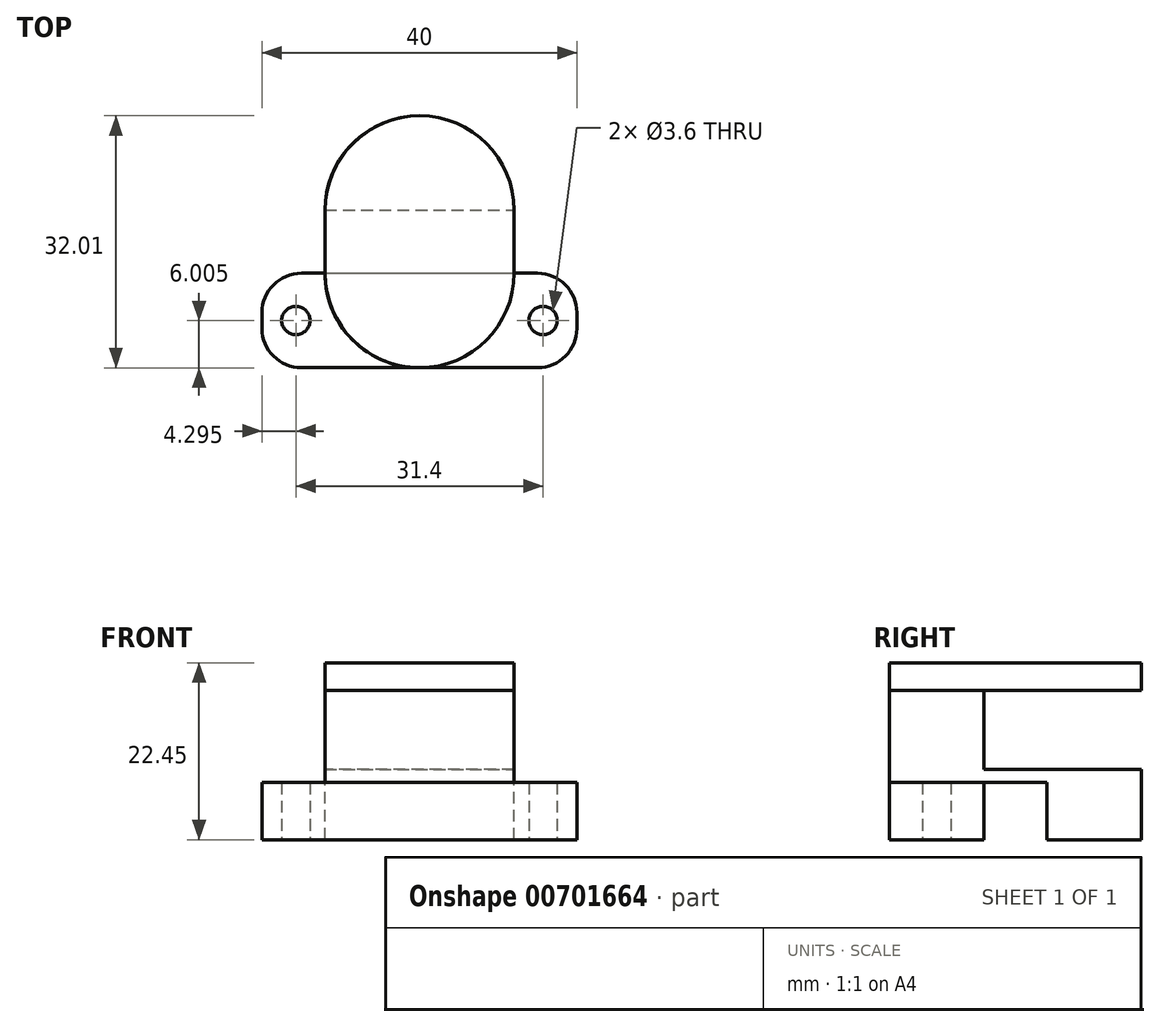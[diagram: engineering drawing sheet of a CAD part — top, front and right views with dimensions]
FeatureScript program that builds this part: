
annotation { "Feature Type Name" : "Feature", "Feature Type Description" : "" }
export const myFeature = defineFeature(function(context is Context, id is Id, definition is map)
    precondition{}
    {
        {
            var Q0;
            Q0=qCreatedBy(makeId("Top.planeOp"),FACE);
            var sketch = newSketch(context, id + "F0", { "sketchPlane" : qUnion([Q0])});
            skLineSegment(sketch, "E0.bottom", {"start": v(-15.42, -8.49) * mm, "end": v(14.58, -8.49) * mm});
            skLineSegment(sketch, "E0.top", {"start": v(-15.42, -20.49) * mm, "end": v(14.58, -20.49) * mm});
            skLineSegment(sketch, "E0.left", {"start": v(-20.42, -13.49) * mm, "end": v(-20.42, -15.49) * mm});
            skLineSegment(sketch, "E0.right", {"start": v(19.58, -13.49) * mm, "end": v(19.58, -15.49) * mm});
            skPoint(sketch, "E1.visualSharp", {"position": v(-20.42, -20.49) * mm});
            skArc(sketch, "E1.filletArc", {"start": v(-20.42, -15.49) * mm, "mid": v(-18.96, -19.02) * mm, "end": v(-15.42, -20.49) * mm});
            skPoint(sketch, "E2.visualSharp", {"position": v(-20.42, -8.49) * mm});
            skArc(sketch, "E2.filletArc", {"start": v(-15.42, -8.49) * mm, "mid": v(-18.96, -9.95) * mm, "end": v(-20.42, -13.49) * mm});
            skPoint(sketch, "E3.visualSharp", {"position": v(19.58, -20.49) * mm});
            skArc(sketch, "E3.filletArc", {"start": v(14.58, -20.49) * mm, "mid": v(18.11, -19.02) * mm, "end": v(19.58, -15.49) * mm});
            skPoint(sketch, "E4.visualSharp", {"position": v(19.58, -8.49) * mm});
            skArc(sketch, "E4.filletArc", {"start": v(19.58, -13.49) * mm, "mid": v(18.11, -9.95) * mm, "end": v(14.58, -8.49) * mm});
            skPoint(sketch, "E5.centerSnap0", {"position": v(-20.42, -14.49) * mm});
            skCircle(sketch, "E6", {"center": v(-16.12, -14.49) * mm, "radius": 1.8 * mm});
            skCircle(sketch, "E7", {"center": v(15.28, -14.49) * mm, "radius": 1.8 * mm});
            skSolve(sketch);
        }
        {
            var Q0;
            Q0 = qSketchRegion(id + "F0", true);
            extrude(context, id + "F1", {"entities" : qUnion([Q0]), "depth" : 7.25 * mm, "offsetDistance" : 25 * mm});
        }
        {
            var Q0;
            Q0=makeQuery(id+"F1.opExtrude","CAP_FACE",FACE,{"disambiguationData":[OSD([sQuery(id+"F0.wireOp",EDGE,"E0.bottom"),sQuery(id+"F0.wireOp",EDGE,"E0.top"),sQuery(id+"F0.wireOp",EDGE,"E0.left"),sQuery(id+"F0.wireOp",EDGE,"E0.right"),sQuery(id+"F0.wireOp",EDGE,"E1.filletArc"),sQuery(id+"F0.wireOp",EDGE,"E2.filletArc"),sQuery(id+"F0.wireOp",EDGE,"E3.filletArc"),sQuery(id+"F0.wireOp",EDGE,"E4.filletArc"),sQuery(id+"F0.wireOp",EDGE,"E6"),sQuery(id+"F0.wireOp",EDGE,"E7")])],"isStart":false});
            var sketch = newSketch(context, id + "F2", { "sketchPlane" : qUnion([Q0])});
            skLineSegment(sketch, "E8.bottom", {"start": v(-0.42, -20.49) * mm, "end": v(-0.42, -20.49) * mm});
            skLineSegment(sketch, "E8.top", {"start": v(-0.42, 11.51) * mm, "end": v(-0.42, 11.51) * mm});
            skLineSegment(sketch, "E8.left", {"start": v(-12.42, -8.49) * mm, "end": v(-12.42, -0.49) * mm});
            skLineSegment(sketch, "E8.right", {"start": v(11.58, -8.49) * mm, "end": v(11.58, -0.49) * mm});
            skPoint(sketch, "E9.visualSharp", {"position": v(-12.42, 11.51) * mm});
            skArc(sketch, "E9.filletArc", {"start": v(-0.42, 11.51) * mm, "mid": v(-8.91, 8) * mm, "end": v(-12.42, -0.49) * mm});
            skPoint(sketch, "E10.visualSharp", {"position": v(11.58, 11.51) * mm});
            skArc(sketch, "E10.filletArc", {"start": v(11.58, -0.49) * mm, "mid": v(8.06, 8) * mm, "end": v(-0.42, 11.51) * mm});
            skPoint(sketch, "E11.visualSharp", {"position": v(-12.42, -20.49) * mm});
            skArc(sketch, "E11.filletArc", {"start": v(-12.42, -8.49) * mm, "mid": v(-8.91, -16.97) * mm, "end": v(-0.42, -20.49) * mm});
            skPoint(sketch, "E12.visualSharp", {"position": v(11.58, -20.49) * mm});
            skArc(sketch, "E12.filletArc", {"start": v(-0.42, -20.49) * mm, "mid": v(8.06, -16.97) * mm, "end": v(11.58, -8.49) * mm});
            skSolve(sketch);
        }
        {
            var Q0;
            Q0 = qSketchRegion(id + "F2", true);
            extrude(context, id + "F3", {"entities" : qUnion([Q0]), "operationType" : NewBodyOperationType.ADD, "depth" : 1.7 * mm, "offsetDistance" : 25 * mm});
        }
        {
            var Q0;
            Q0=makeQuery(id+"F3.opExtrude","CAP_FACE",FACE,{"disambiguationData":[OSD([sQuery(id+"F2.wireOp",EDGE,"E8.left"),sQuery(id+"F2.wireOp",EDGE,"E8.right"),sQuery(id+"F2.wireOp",EDGE,"E9.filletArc"),sQuery(id+"F2.wireOp",EDGE,"E10.filletArc"),sQuery(id+"F2.wireOp",EDGE,"E11.filletArc"),sQuery(id+"F2.wireOp",EDGE,"E12.filletArc")])],"isStart":true});
            var sketch = newSketch(context, id + "F4", { "sketchPlane" : qUnion([Q0])});
            skLineSegment(sketch, "E13", {"start": v(-12.42, 0.49) * mm, "end": v(11.58, 0.49) * mm});
            skArc(sketch, "E14", {"start": v(-12.42, 0.49) * mm, "mid": v(-0.42, -11.51) * mm, "end": v(11.58, 0.49) * mm});
            skSolve(sketch);
        }
        {
            var Q0;
            Q0 = qSketchRegion(id + "F4", true);
            extrude(context, id + "F5", {"entities" : qUnion([Q0]), "operationType" : NewBodyOperationType.ADD, "depth" : 7.25 * mm, "offsetDistance" : 25 * mm});
        }
        {
            var Q0;
            Q0=makeQuery(id+"F3.opExtrude","CAP_FACE",FACE,{"disambiguationData":[OSD([sQuery(id+"F2.wireOp",EDGE,"E8.left"),sQuery(id+"F2.wireOp",EDGE,"E8.right"),sQuery(id+"F2.wireOp",EDGE,"E9.filletArc"),sQuery(id+"F2.wireOp",EDGE,"E10.filletArc"),sQuery(id+"F2.wireOp",EDGE,"E11.filletArc"),sQuery(id+"F2.wireOp",EDGE,"E12.filletArc")])],"isStart":false});
            var sketch = newSketch(context, id + "F6", { "sketchPlane" : qUnion([Q0])});
            skLineSegment(sketch, "E15", {"start": v(-12.42, -8.49) * mm, "end": v(11.58, -8.49) * mm});
            skArc(sketch, "E16", {"start": v(-12.42, -8.49) * mm, "mid": v(-0.42, -20.49) * mm, "end": v(11.58, -8.49) * mm});
            skSolve(sketch);
        }
        {
            var Q0;
            Q0=makeQuery(id+"F6.imprint","IMPRINT",FACE,{"disambiguationData":[TD([[makeQuery(id+"F6.imprint","IMPRINT",EDGE,{"derivedFrom":sQuery(id+"F6.wireOp",EDGE,"E15")}),-1.0]])]});
            extrude(context, id + "F7", {"entities" : qUnion([Q0]), "operationType" : NewBodyOperationType.ADD, "depth" : 10 * mm, "offsetDistance" : 25 * mm});
        }
        {
            var Q0;
            Q0=makeQuery(id+"F7.opExtrude","CAP_FACE",FACE,{"disambiguationData":[OSD([sQuery(id+"F6.wireOp",EDGE,"E15"),sQuery(id+"F6.wireOp",EDGE,"E16")])],"isStart":false});
            var sketch = newSketch(context, id + "F8", { "sketchPlane" : qUnion([Q0])});
            skLineSegment(sketch, "E17.bottom", {"start": v(-0.4, 11.52) * mm, "end": v(-0.4, 11.52) * mm});
            skLineSegment(sketch, "E17.top", {"start": v(-0.4, -20.48) * mm, "end": v(-0.4, -20.48) * mm});
            skLineSegment(sketch, "E17.left", {"start": v(-12.4, -0.48) * mm, "end": v(-12.4, -8.48) * mm});
            skLineSegment(sketch, "E17.right", {"start": v(11.6, -0.48) * mm, "end": v(11.6, -8.48) * mm});
            skPoint(sketch, "E18.visualSharp", {"position": v(-12.4, 11.52) * mm});
            skArc(sketch, "E18.filletArc", {"start": v(-0.4, 11.52) * mm, "mid": v(-8.88, 8) * mm, "end": v(-12.4, -0.48) * mm});
            skPoint(sketch, "E19.visualSharp", {"position": v(11.6, 11.52) * mm});
            skArc(sketch, "E19.filletArc", {"start": v(11.6, -0.48) * mm, "mid": v(8.1, 8) * mm, "end": v(-0.4, 11.52) * mm});
            skPoint(sketch, "E20.visualSharp", {"position": v(-12.4, -20.48) * mm});
            skArc(sketch, "E20.filletArc", {"start": v(-12.4, -8.48) * mm, "mid": v(-8.88, -16.97) * mm, "end": v(-0.4, -20.48) * mm});
            skPoint(sketch, "E21.visualSharp", {"position": v(11.6, -20.48) * mm});
            skArc(sketch, "E21.filletArc", {"start": v(-0.4, -20.48) * mm, "mid": v(8.1, -16.97) * mm, "end": v(11.6, -8.48) * mm});
            skSolve(sketch);
        }
        {
            var Q0;
            Q0 = qSketchRegion(id + "F8", true);
            extrude(context, id + "F9", {"entities" : qUnion([Q0]), "operationType" : NewBodyOperationType.ADD, "depth" : 3.5 * mm, "offsetDistance" : 25 * mm});
        }
    });
